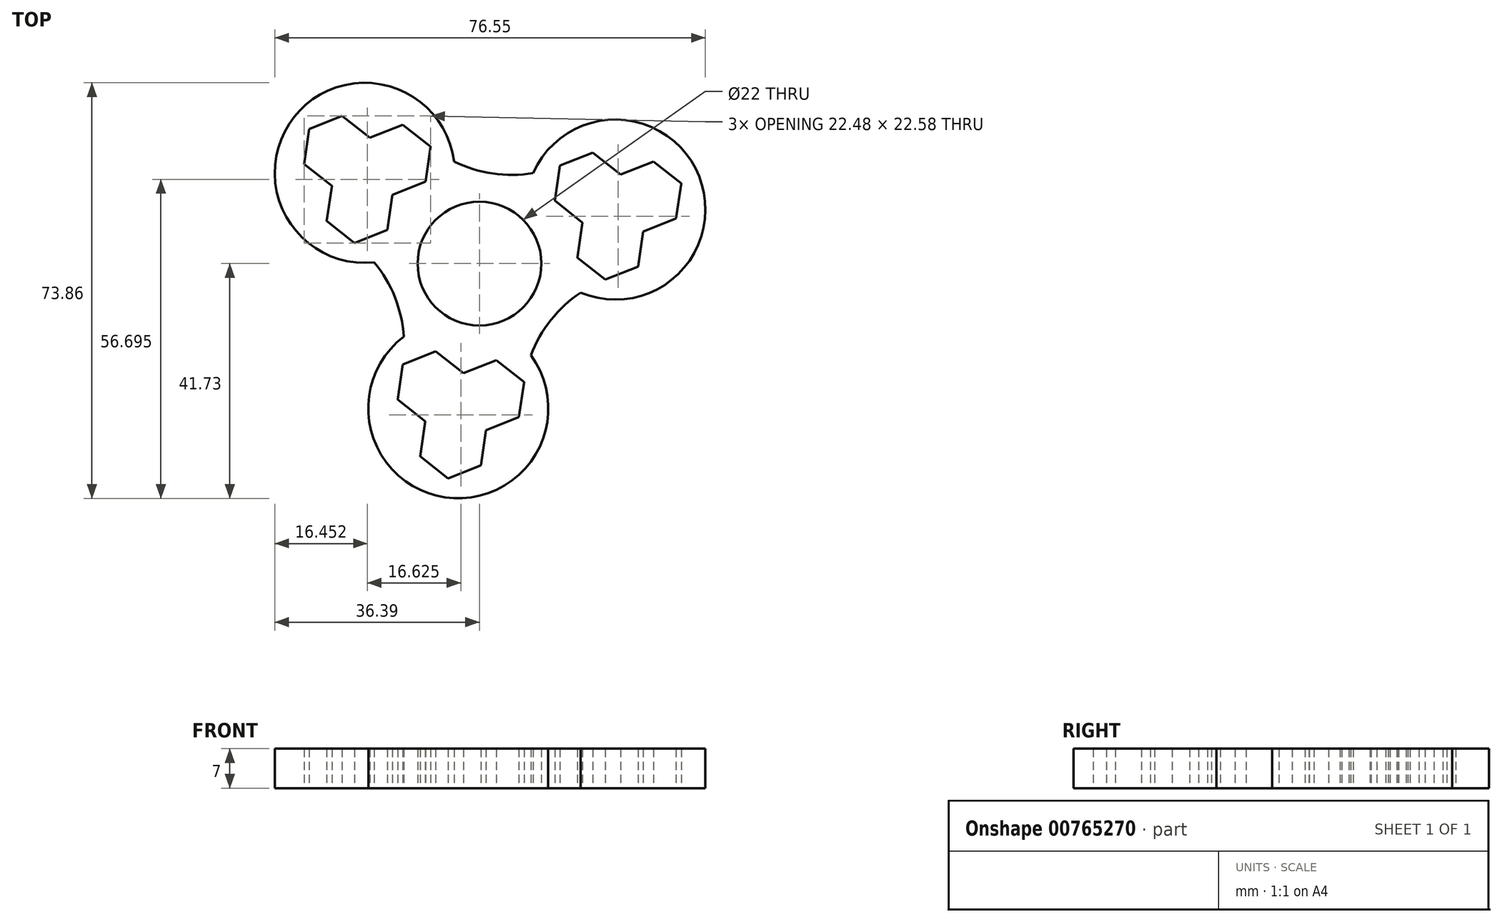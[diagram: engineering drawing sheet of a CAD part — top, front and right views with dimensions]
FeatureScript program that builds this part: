
annotation { "Feature Type Name" : "Feature", "Feature Type Description" : "" }
export const myFeature = defineFeature(function(context is Context, id is Id, definition is map)
    precondition{}
    {
        {
            var Q0;
            Q0=qCreatedBy(makeId("Top.planeOp"),FACE);
            var sketch = newSketch(context, id + "F0", { "sketchPlane" : qUnion([Q0])});
            skCircle(sketch, "E0", {"center": v(0, 0) * mm, "radius": 15 * mm});
            skCircle(sketch, "E1", {"center": v(0, 0) * mm, "radius": 11 * mm});
            skLineSegment(sketch, "E2", {"start": v(0, 0) * mm, "end": v(-20.4, 16.13) * mm});
            skLineSegment(sketch, "E3", {"start": v(0, 0) * mm, "end": v(24.16, 9.6) * mm});
            skLineSegment(sketch, "E4", {"start": v(0, 0) * mm, "end": v(-3.77, -25.73) * mm});
            skPoint(sketch, "E5.0.midPoint", {"position": v(-16.08, 12.72) * mm});
            skPoint(sketch, "E6.0.midPoint", {"position": v(19.05, 7.57) * mm});
            skPoint(sketch, "E7.0.midPoint", {"position": v(-2.97, -20.28) * mm});
            skCircle(sketch, "E8", {"center": v(-3.77, -25.73) * mm, "radius": 16 * mm});
            skCircle(sketch, "E9", {"center": v(-20.4, 16.13) * mm, "radius": 16 * mm});
            skCircle(sketch, "E10", {"center": v(24.16, 9.6) * mm, "radius": 16 * mm});
            skCircle(sketch, "E11.cCircle", {"center": v(-25.33, 20.03) * mm, "radius": 6.3 * mm, "construction": true});
            skLineSegment(sketch, "E11.0", {"start": v(-19.48, 22.35) * mm, "end": v(-20.4, 16.13) * mm});
            skLineSegment(sketch, "E11.1", {"start": v(-20.4, 16.13) * mm, "end": v(-26.24, 13.8) * mm});
            skLineSegment(sketch, "E11.2", {"start": v(-26.24, 13.8) * mm, "end": v(-31.18, 17.7) * mm});
            skLineSegment(sketch, "E11.3", {"start": v(-31.18, 17.7) * mm, "end": v(-30.27, 23.93) * mm});
            skLineSegment(sketch, "E11.4", {"start": v(-30.27, 23.93) * mm, "end": v(-24.42, 26.26) * mm});
            skLineSegment(sketch, "E11.5", {"start": v(-24.42, 26.26) * mm, "end": v(-19.48, 22.35) * mm});
            skCircle(sketch, "E12.cCircle", {"center": v(-14.55, 18.45) * mm, "radius": 6.3 * mm, "construction": true});
            skLineSegment(sketch, "E12.0", {"start": v(-8.7, 20.77) * mm, "end": v(-9.6, 14.55) * mm});
            skLineSegment(sketch, "E12.1", {"start": v(-9.6, 14.55) * mm, "end": v(-15.46, 12.22) * mm});
            skLineSegment(sketch, "E12.2", {"start": v(-15.46, 12.22) * mm, "end": v(-20.4, 16.13) * mm});
            skLineSegment(sketch, "E12.3", {"start": v(-20.4, 16.13) * mm, "end": v(-19.48, 22.35) * mm});
            skLineSegment(sketch, "E12.4", {"start": v(-19.48, 22.35) * mm, "end": v(-13.63, 24.68) * mm});
            skLineSegment(sketch, "E12.5", {"start": v(-13.63, 24.68) * mm, "end": v(-8.7, 20.77) * mm});
            skCircle(sketch, "E13.cCircle", {"center": v(-21.3, 9.9) * mm, "radius": 6.3 * mm, "construction": true});
            skLineSegment(sketch, "E13.0", {"start": v(-16.37, 6) * mm, "end": v(-22.22, 3.67) * mm});
            skLineSegment(sketch, "E13.1", {"start": v(-22.22, 3.67) * mm, "end": v(-27.16, 7.58) * mm});
            skLineSegment(sketch, "E13.2", {"start": v(-27.16, 7.58) * mm, "end": v(-26.24, 13.8) * mm});
            skLineSegment(sketch, "E13.3", {"start": v(-26.24, 13.8) * mm, "end": v(-20.4, 16.13) * mm});
            skLineSegment(sketch, "E13.4", {"start": v(-20.4, 16.13) * mm, "end": v(-15.46, 12.22) * mm});
            skLineSegment(sketch, "E13.5", {"start": v(-15.46, 12.22) * mm, "end": v(-16.37, 6) * mm});
            skCircle(sketch, "E14.MirrorC", {"center": v(30.01, 11.92) * mm, "radius": 6.3 * mm, "construction": true});
            skCircle(sketch, "E15.MirrorC", {"center": v(19.23, 13.5) * mm, "radius": 6.3 * mm, "construction": true});
            skCircle(sketch, "E16.MirrorC", {"center": v(23.25, 3.37) * mm, "radius": 6.3 * mm, "construction": true});
            skLineSegment(sketch, "E17.MirrorCS", {"start": v(30.92, 18.15) * mm, "end": v(25.08, 15.82) * mm});
            skLineSegment(sketch, "E18.MirrorCS", {"start": v(35.86, 14.24) * mm, "end": v(30.92, 18.15) * mm});
            skLineSegment(sketch, "E19.MirrorCS", {"start": v(34.95, 8.02) * mm, "end": v(35.86, 14.24) * mm});
            skLineSegment(sketch, "E20.MirrorCS", {"start": v(29.1, 5.7) * mm, "end": v(34.95, 8.02) * mm});
            skLineSegment(sketch, "E21.MirrorCS", {"start": v(24.16, 9.6) * mm, "end": v(29.1, 5.7) * mm});
            skLineSegment(sketch, "E22.MirrorCS", {"start": v(25.08, 15.82) * mm, "end": v(24.16, 9.6) * mm});
            skLineSegment(sketch, "E23.MirrorCS", {"start": v(25.08, 15.82) * mm, "end": v(20.14, 19.73) * mm});
            skLineSegment(sketch, "E24.MirrorCS", {"start": v(20.14, 19.73) * mm, "end": v(14.3, 17.4) * mm});
            skLineSegment(sketch, "E25.MirrorCS", {"start": v(14.3, 17.4) * mm, "end": v(13.38, 11.18) * mm});
            skLineSegment(sketch, "E26.MirrorCS", {"start": v(13.38, 11.18) * mm, "end": v(18.31, 7.28) * mm});
            skLineSegment(sketch, "E27.MirrorCS", {"start": v(18.31, 7.28) * mm, "end": v(24.16, 9.6) * mm});
            skLineSegment(sketch, "E28.MirrorCS", {"start": v(28.19, -0.53) * mm, "end": v(29.1, 5.7) * mm});
            skLineSegment(sketch, "E29.MirrorCS", {"start": v(22.34, -2.85) * mm, "end": v(28.19, -0.53) * mm});
            skLineSegment(sketch, "E30.MirrorCS", {"start": v(17.4, 1.05) * mm, "end": v(22.34, -2.85) * mm});
            skLineSegment(sketch, "E31.MirrorCS", {"start": v(18.31, 7.28) * mm, "end": v(17.4, 1.05) * mm});
            skLineSegment(sketch, "E32.MirrorCS", {"start": v(-14.55, -24.15) * mm, "end": v(-13.64, -17.92) * mm});
            skLineSegment(sketch, "E33.MirrorCS", {"start": v(-9.62, -28.05) * mm, "end": v(-14.55, -24.15) * mm});
            skLineSegment(sketch, "E34.MirrorCS", {"start": v(-13.64, -17.92) * mm, "end": v(-7.8, -15.6) * mm});
            skLineSegment(sketch, "E35.MirrorCS", {"start": v(-9.62, -28.05) * mm, "end": v(-3.77, -25.73) * mm});
            skLineSegment(sketch, "E36.MirrorCS", {"start": v(-10.53, -34.28) * mm, "end": v(-9.62, -28.05) * mm});
            skLineSegment(sketch, "E37.MirrorCS", {"start": v(-5.6, -38.18) * mm, "end": v(-10.53, -34.28) * mm});
            skLineSegment(sketch, "E38.MirrorCS", {"start": v(0.25, -35.86) * mm, "end": v(-5.6, -38.18) * mm});
            skLineSegment(sketch, "E39.MirrorCS", {"start": v(1.17, -29.63) * mm, "end": v(0.25, -35.86) * mm});
            skLineSegment(sketch, "E40.MirrorCS", {"start": v(-3.77, -25.73) * mm, "end": v(1.17, -29.63) * mm});
            skLineSegment(sketch, "E41.MirrorCS", {"start": v(-2.86, -19.5) * mm, "end": v(3, -17.18) * mm});
            skLineSegment(sketch, "E42.MirrorCS", {"start": v(7.02, -27.3) * mm, "end": v(1.17, -29.63) * mm});
            skLineSegment(sketch, "E43.MirrorCS", {"start": v(7.93, -21.08) * mm, "end": v(7.02, -27.3) * mm});
            skLineSegment(sketch, "E44.MirrorCS", {"start": v(3, -17.18) * mm, "end": v(7.93, -21.08) * mm});
            skLineSegment(sketch, "E45.MirrorCS", {"start": v(-7.8, -15.6) * mm, "end": v(-2.86, -19.5) * mm});
            skCircle(sketch, "E46.MirrorC", {"center": v(-8.7, -21.82) * mm, "radius": 6.3 * mm, "construction": true});
            skCircle(sketch, "E47.MirrorC", {"center": v(-4.68, -31.95) * mm, "radius": 6.3 * mm, "construction": true});
            skCircle(sketch, "E48.MirrorC", {"center": v(2.08, -23.4) * mm, "radius": 6.3 * mm, "construction": true});
            skLineSegment(sketch, "E49", {"start": v(-8.7, 20.77) * mm, "end": v(14.3, 17.4) * mm, "construction": true});
            skLineSegment(sketch, "E50", {"start": v(22.34, -2.85) * mm, "end": v(7.93, -21.08) * mm, "construction": true});
            skLineSegment(sketch, "E51", {"start": v(-13.64, -17.92) * mm, "end": v(-22.22, 3.67) * mm, "construction": true});
            skArc(sketch, "E52", {"start": v(-8.7, 20.77) * mm, "mid": v(2.35, 16) * mm, "end": v(14.3, 17.4) * mm});
            skArc(sketch, "E53", {"start": v(22.34, -2.85) * mm, "mid": v(12.7, -10.04) * mm, "end": v(7.93, -21.08) * mm});
            skArc(sketch, "E54", {"start": v(-13.64, -17.92) * mm, "mid": v(-15.04, -5.97) * mm, "end": v(-22.22, 3.67) * mm});
            skSolve(sketch);
        }
        {
            var Q0;
            Q0=qSketchRegion(id+"F0",true);
            var Q1;
            {var subQ5=sQuery(id+"F0.wireOp",EDGE,"E10");var subQ6=sQuery(id+"F0.wireOp",EDGE,"E0");var subQ7=makeQuery(id+"F0.imprint","INTERSECT",VERTEX,{"disambiguationData":[OD(1.0)],"derivedFrom":[subQ6,subQ5]});Q1=makeQuery(id+"F0.imprint","IMPRINT",FACE,{"disambiguationData":[TD([[makeQuery(id+"F0.imprint","IMPRINT",EDGE,{"disambiguationData":[TD([[subQ7,-1.0]])],"derivedFrom":subQ6}),1.0]])]});}
            var Q2;
            {var subQ3=sQuery(id+"F0.wireOp",EDGE,"E10");var subQ6=sQuery(id+"F0.wireOp",EDGE,"E0");var subQ10=makeQuery(id+"F0.imprint","INTERSECT",VERTEX,{"disambiguationData":[OD(0.0)],"derivedFrom":[subQ6,subQ3]});Q2=makeQuery(id+"F0.imprint","IMPRINT",FACE,{"disambiguationData":[TD([[makeQuery(id+"F0.imprint","IMPRINT",EDGE,{"disambiguationData":[TD([[subQ10,1.0]])],"derivedFrom":subQ6}),1.0]])]});}
            var Q3;
            {var subQ1=sQuery(id+"F0.wireOp",EDGE,"E0");var subQ8=sQuery(id+"F0.wireOp",EDGE,"E9");var subQ11=makeQuery(id+"F0.imprint","INTERSECT",VERTEX,{"disambiguationData":[OD(1.0)],"derivedFrom":[subQ1,subQ8]});Q3=makeQuery(id+"F0.imprint","IMPRINT",FACE,{"disambiguationData":[TD([[makeQuery(id+"F0.imprint","IMPRINT",EDGE,{"disambiguationData":[TD([[subQ11,-1.0]])],"derivedFrom":subQ1}),1.0]])]});}
            var Q4;
            {var subQ0=sQuery(id+"F0.wireOp",EDGE,"E2");var subQ1=sQuery(id+"F0.wireOp",EDGE,"E0");var subQ2=makeQuery(id+"F0.imprint","INTERSECT",VERTEX,{"derivedFrom":[subQ1,subQ0]});Q4=makeQuery(id+"F0.imprint","IMPRINT",FACE,{"disambiguationData":[TD([[makeQuery(id+"F0.imprint","IMPRINT",EDGE,{"disambiguationData":[TD([[subQ2,-1.0]])],"derivedFrom":subQ1}),1.0]])]});}
            var Q5;
            {var subQ0=sQuery(id+"F0.wireOp",EDGE,"E9");var subQ1=sQuery(id+"F0.wireOp",EDGE,"E0");var subQ2=makeQuery(id+"F0.imprint","INTERSECT",VERTEX,{"disambiguationData":[OD(0.0)],"derivedFrom":[subQ1,subQ0]});Q5=makeQuery(id+"F0.imprint","IMPRINT",FACE,{"disambiguationData":[TD([[makeQuery(id+"F0.imprint","IMPRINT",EDGE,{"disambiguationData":[TD([[subQ2,-1.0]])],"derivedFrom":subQ1}),1.0]])]});}
            var Q6;
            {var subQ0=sQuery(id+"F0.wireOp",EDGE,"E3");var subQ1=sQuery(id+"F0.wireOp",EDGE,"E0");var subQ2=makeQuery(id+"F0.imprint","INTERSECT",VERTEX,{"derivedFrom":[subQ1,subQ0]});Q6=makeQuery(id+"F0.imprint","IMPRINT",FACE,{"disambiguationData":[TD([[makeQuery(id+"F0.imprint","IMPRINT",EDGE,{"disambiguationData":[TD([[subQ2,-1.0]])],"derivedFrom":subQ1}),1.0]])]});}
            var Q7;
            {var subQ0=sQuery(id+"F0.wireOp",EDGE,"E3");var subQ1=sQuery(id+"F0.wireOp",EDGE,"E0");var subQ2=makeQuery(id+"F0.imprint","INTERSECT",VERTEX,{"derivedFrom":[subQ1,subQ0]});Q7=makeQuery(id+"F0.imprint","IMPRINT",FACE,{"disambiguationData":[TD([[makeQuery(id+"F0.imprint","IMPRINT",EDGE,{"disambiguationData":[TD([[subQ2,1.0]])],"derivedFrom":subQ1}),1.0]])]});}
            var Q8;
            {var subQ0=sQuery(id+"F0.wireOp",EDGE,"E8");var subQ1=sQuery(id+"F0.wireOp",EDGE,"E0");var subQ2=makeQuery(id+"F0.imprint","INTERSECT",VERTEX,{"disambiguationData":[OD(0.0)],"derivedFrom":[subQ1,subQ0]});Q8=makeQuery(id+"F0.imprint","IMPRINT",FACE,{"disambiguationData":[TD([[makeQuery(id+"F0.imprint","IMPRINT",EDGE,{"disambiguationData":[TD([[subQ2,-1.0]])],"derivedFrom":subQ1}),1.0]])]});}
            var Q9;
            {var subQ0=sQuery(id+"F0.wireOp",EDGE,"E4");var subQ1=sQuery(id+"F0.wireOp",EDGE,"E0");var subQ2=makeQuery(id+"F0.imprint","INTERSECT",VERTEX,{"derivedFrom":[subQ1,subQ0]});Q9=makeQuery(id+"F0.imprint","IMPRINT",FACE,{"disambiguationData":[TD([[makeQuery(id+"F0.imprint","IMPRINT",EDGE,{"disambiguationData":[TD([[subQ2,-1.0]])],"derivedFrom":subQ1}),1.0]])]});}
            var Q10;
            {var subQ3=sQuery(id+"F0.wireOp",EDGE,"E10");var subQ6=sQuery(id+"F0.wireOp",EDGE,"E0");var subQ11=makeQuery(id+"F0.imprint","INTERSECT",VERTEX,{"disambiguationData":[OD(0.0)],"derivedFrom":[subQ6,subQ3]});Q10=makeQuery(id+"F0.imprint","IMPRINT",FACE,{"disambiguationData":[TD([[makeQuery(id+"F0.imprint","IMPRINT",EDGE,{"disambiguationData":[TD([[subQ11,-1.0]])],"derivedFrom":subQ6}),1.0]])]});}
            var Q11;
            {var subQ0=sQuery(id+"F0.wireOp",EDGE,"E8");var subQ1=sQuery(id+"F0.wireOp",EDGE,"E0");var subQ2=makeQuery(id+"F0.imprint","INTERSECT",VERTEX,{"disambiguationData":[OD(1.0)],"derivedFrom":[subQ1,subQ0]});Q11=makeQuery(id+"F0.imprint","IMPRINT",FACE,{"disambiguationData":[TD([[makeQuery(id+"F0.imprint","IMPRINT",EDGE,{"disambiguationData":[TD([[subQ2,-1.0]])],"derivedFrom":subQ1}),1.0]])]});}
            extrude(context, id + "F1", {"entities" : qUnion([Q0, Q1, Q2, Q3, Q4, Q5, Q6, Q7, Q8, Q9, Q10, Q11]), "depth" : 7 * mm});
        }
    });
